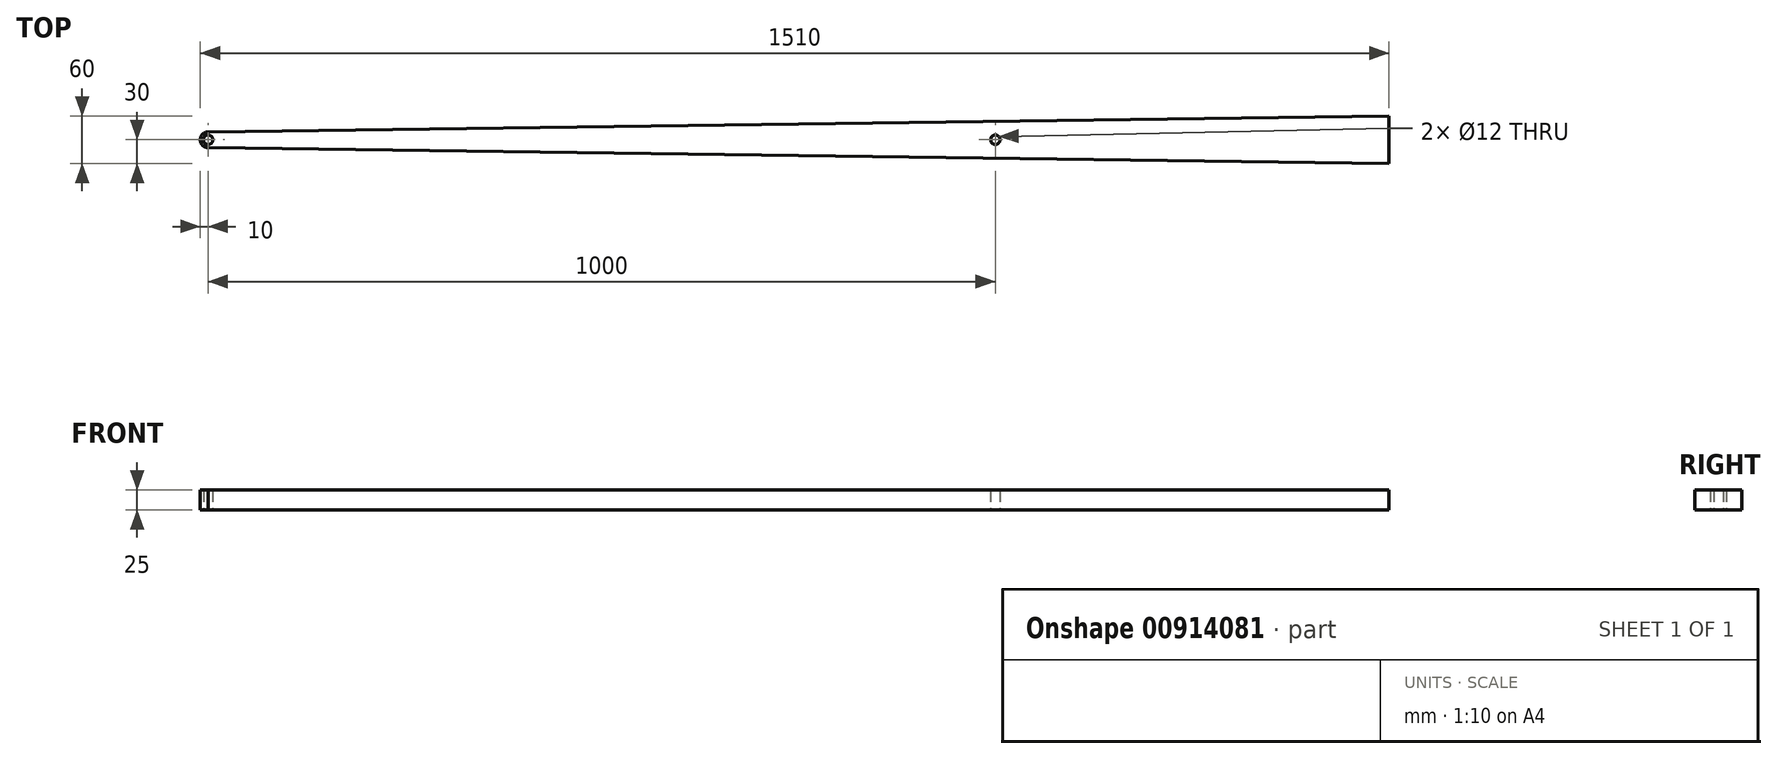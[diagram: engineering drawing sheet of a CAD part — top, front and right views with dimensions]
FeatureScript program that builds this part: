
annotation { "Feature Type Name" : "Feature", "Feature Type Description" : "" }
export const myFeature = defineFeature(function(context is Context, id is Id, definition is map)
    precondition{}
    {
        {
            var Q0;
            Q0=qCreatedBy(makeId("Top.planeOp"),FACE);
            var sketch = newSketch(context, id + "F0", { "sketchPlane" : qUnion([Q0])});
            skCircle(sketch, "E0", {"center": v(0, 0) * mm, "radius": 6 * mm});
            skLineSegment(sketch, "E1", {"start": v(-304.1, 0) * mm, "end": v(1724.45, 0) * mm, "construction": true});
            skLineSegment(sketch, "E2", {"start": v(0, 345.05) * mm, "end": v(0, -379.86) * mm, "construction": true});
            skCircle(sketch, "E3", {"center": v(0, 0) * mm, "radius": 10 * mm});
            skLineSegment(sketch, "E4", {"start": v(1500, 0) * mm, "end": v(1500, -30) * mm});
            skLineSegment(sketch, "E5.MirrorCS", {"start": v(1500, 0) * mm, "end": v(1500, 30) * mm});
            skLineSegment(sketch, "E6", {"start": v(1500, 30) * mm, "end": v(0, 10) * mm});
            skLineSegment(sketch, "E7.MirrorCS", {"start": v(1500, -30) * mm, "end": v(0, -10) * mm});
            skCircle(sketch, "E8", {"center": v(1000, 0) * mm, "radius": 6 * mm});
            skSolve(sketch);
        }
        {
            var Q0;
            Q0 = qSketchRegion(id + "F0", true);
            extrude(context, id + "F1", {"entities" : qUnion([Q0]), "depth" : 25 * mm, "offsetDistance" : 25 * mm});
        }
    });
